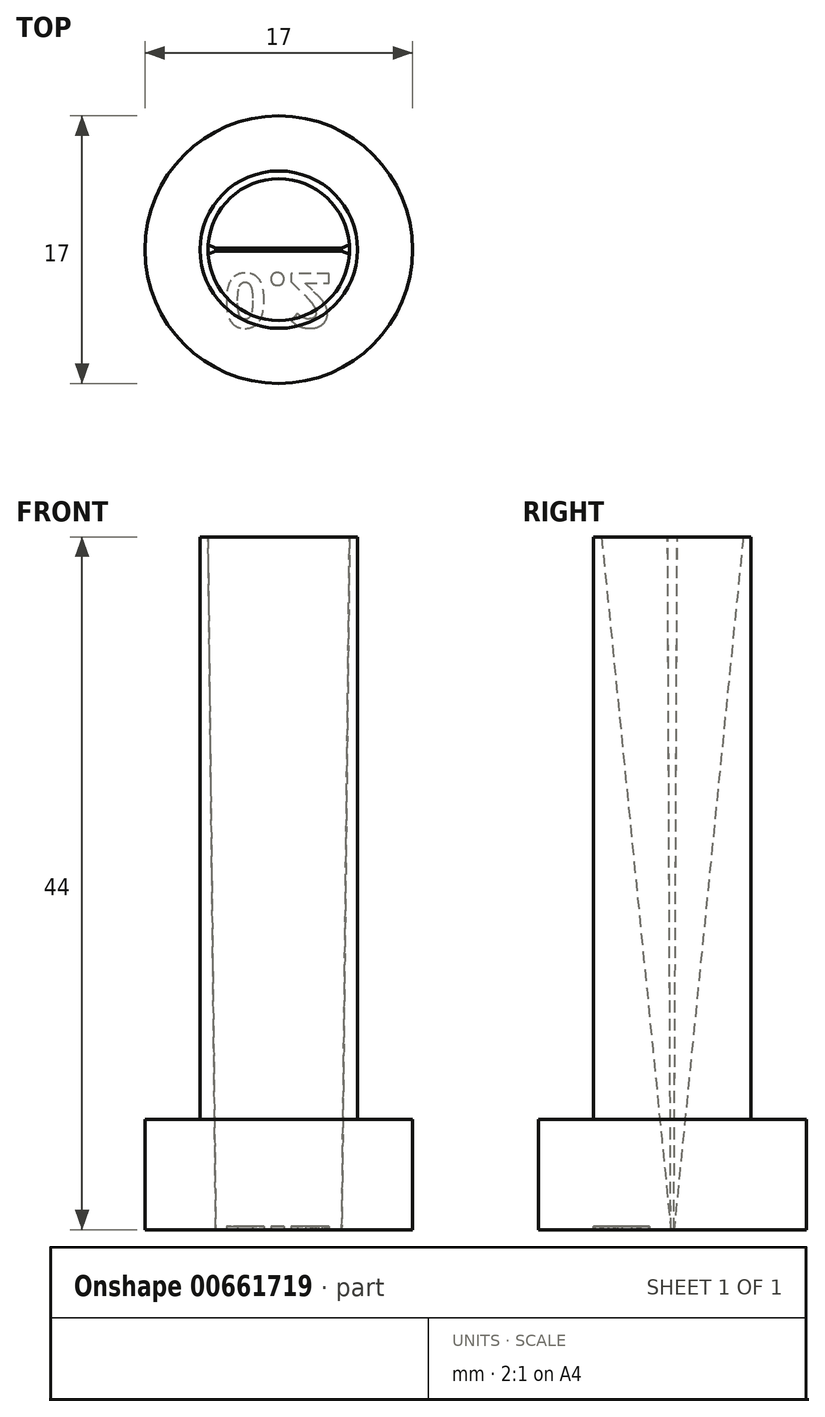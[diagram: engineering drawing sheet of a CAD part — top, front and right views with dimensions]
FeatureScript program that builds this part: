
annotation { "Feature Type Name" : "Feature", "Feature Type Description" : "" }
export const myFeature = defineFeature(function(context is Context, id is Id, definition is map)
    precondition{}
    {
        {
            var Q0;
            Q0=qCreatedBy(makeId("Top.planeOp"),FACE);
            var sketch = newSketch(context, id + "F0", { "sketchPlane" : qUnion([Q0])});
            skCircle(sketch, "E0", {"center": v(0, 0) * mm, "radius": 8.5 * mm});
            skSolve(sketch);
        }
        {
            var Q0;
            Q0=makeQuery(id+"F0.imprint","IMPRINT",FACE,{"disambiguationData":[TD([[makeQuery(id+"F0.imprint","IMPRINT",EDGE,{"derivedFrom":sQuery(id+"F0.wireOp",EDGE,"E0")}),1.0]])]});
            extrude(context, id + "F1", {"entities" : qUnion([Q0]), "depth" : 7 * mm});
        }
        {
            var Q0;
            Q0=makeQuery(id+"F1.opExtrude","CAP_FACE",FACE,{"disambiguationData":[OSD([sQuery(id+"F0.wireOp",EDGE,"E0")])],"isStart":false});
            var sketch = newSketch(context, id + "F2", { "sketchPlane" : qUnion([Q0])});
            skCircle(sketch, "E1", {"center": v(0, 0) * mm, "radius": 5 * mm});
            skSolve(sketch);
        }
        {
            var Q0;
            Q0=makeQuery(id+"F1.opExtrude","CAP_FACE",FACE,{"disambiguationData":[OSD([sQuery(id+"F0.wireOp",EDGE,"E0")])],"isStart":true});
            var sketch = newSketch(context, id + "F3", { "sketchPlane" : qUnion([Q0])});
            skPoint(sketch, "E2.middle", {"position": v(0, 0) * mm});
            skLineSegment(sketch, "E3.bottom", {"start": v(-4, 0.1) * mm, "end": v(4, 0.1) * mm});
            skLineSegment(sketch, "E3.top", {"start": v(-4, -0.1) * mm, "end": v(4, -0.1) * mm});
            skLineSegment(sketch, "E3.left", {"start": v(-4, 0.1) * mm, "end": v(-4, -0.1) * mm});
            skLineSegment(sketch, "E3.right", {"start": v(4, 0.1) * mm, "end": v(4, -0.1) * mm});
            skSolve(sketch);
        }
        {
            var Q0;
            Q0=makeQuery(id+"F2.imprint","IMPRINT",FACE,{"disambiguationData":[TD([[makeQuery(id+"F2.imprint","IMPRINT",EDGE,{"derivedFrom":sQuery(id+"F2.wireOp",EDGE,"E1")}),-1.0]])]});
            cPlane(context, id + "F4", {"entities" : qUnion([Q0]), "cplaneType" : CPlaneType.OFFSET, "offset" : 37 * mm, "width" : 150 * mm, "height" : 150 * mm});
        }
        {
            var Q0;
            Q0=qCreatedBy(id+"F4.planeOp",FACE);
            var sketch = newSketch(context, id + "F5", { "sketchPlane" : qUnion([Q0])});
            skArc(sketch, "E4", {"start": v(-4.49, -0.3) * mm, "mid": v(0, -4.5) * mm, "end": v(4.5, -0.3) * mm});
            skArc(sketch, "E5", {"start": v(4.5, -0.3) * mm, "mid": v(4.5, 0.01) * mm, "end": v(4.49, 0.32) * mm});
            skArc(sketch, "E6", {"start": v(4.49, 0.32) * mm, "mid": v(0, 4.5) * mm, "end": v(-4.49, 0.3) * mm});
            skArc(sketch, "E7", {"start": v(-4.49, 0.3) * mm, "mid": v(-4.5, 0) * mm, "end": v(-4.49, -0.3) * mm});
            skSolve(sketch);
        }
        {
            var Q0;
            Q0=makeQuery(id+"F2.imprint","IMPRINT",FACE,{"disambiguationData":[TD([[makeQuery(id+"F2.imprint","IMPRINT",EDGE,{"derivedFrom":sQuery(id+"F2.wireOp",EDGE,"E1")}),1.0]])]});
            extrude(context, id + "F6", {"entities" : qUnion([Q0]), "operationType" : NewBodyOperationType.ADD, "depth" : 37 * mm});
        }
        {
            var Q1;
            Q1=makeQuery(id+"F3.imprint","IMPRINT",FACE,{"disambiguationData":[TD([[makeQuery(id+"F3.imprint","IMPRINT",EDGE,{"derivedFrom":sQuery(id+"F3.wireOp",EDGE,"E3.bottom")}),-1.0]])]});
            var Q2;
            Q2=makeQuery(id+"F5.imprint","IMPRINT",FACE,{"disambiguationData":[TD([[makeQuery(id+"F5.imprint","IMPRINT",EDGE,{"derivedFrom":sQuery(id+"F5.wireOp",EDGE,"E4")}),1.0]])]});
            loft(context, id + "F7", {"operationType" : NewBodyOperationType.REMOVE, "sheetProfilesArray" : [{ "sheetProfileEntities" : qUnion([Q1]) }, { "sheetProfileEntities" : qUnion([Q2]) }]});
        }
        {
            var Q0;
            Q0=makeQuery(id+"F3.imprint","IMPRINT",FACE,{"disambiguationData":[TD([[makeQuery(id+"F3.imprint","IMPRINT",EDGE,{"derivedFrom":sQuery(id+"F3.wireOp",EDGE,"E3.bottom")}),1.0]])]});
            var sketch = newSketch(context, id + "F8", { "sketchPlane" : qUnion([Q0])});
            skText(sketch, "E8", { "text": "0.2", "fontName": "OpenSans-Bold.ttf"});
            const initialGuessF8  = {"E8": [-0.0035, 0.00153, 1, 0, 0.00345]};
            skSetInitialGuess(sketch, initialGuessF8);
            skSolve(sketch);
        }
        {
            var Q0;
            Q0=qSketchRegion(id+"F8",true);
            extrude(context, id + "F9", {"entities" : qUnion([Q0]), "operationType" : NewBodyOperationType.REMOVE, "oppositeDirection" : true, "depth" : .2 * mm});
        }
    });
